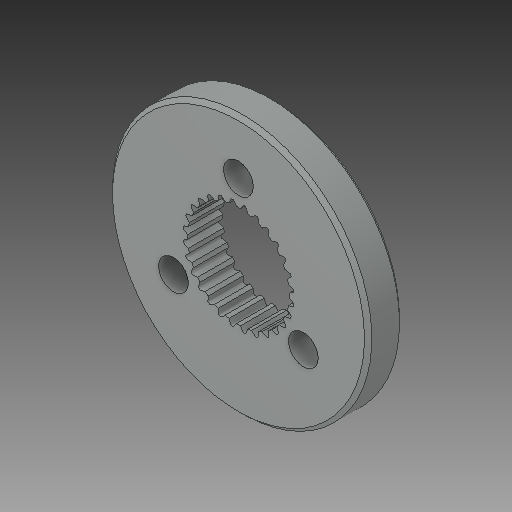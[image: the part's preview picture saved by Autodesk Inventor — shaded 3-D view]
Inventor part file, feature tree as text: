
AUTODESK INVENTOR PART (.ipt)
format: ipt  version: 2018 (Build 220112000, 112)  size: 270,848 bytes
history: native  units: in
note: dims shown in document units (in); Inventor stores cm internally (conversion verified against a paired STEP export)
features: chamfer x1
ambient origin geometry x8: Origin, YZ Plane, XZ Plane, XY Plane, X Axis, Y Axis, Z Axis, Center Point
bodies: Solid1 (feature_tree)
feature tree (1):
  chamfer  "Chamfer1"  [1 undecoded]
note: 1 required parameter value undecoded (feature->parameter linkage not recoverable at this tier; creation-order binding heuristic only, values carry confidence <= 0.55)
